# Revit family: AA-14FBS
name_source: partatom
category: Устройства связи
units: mm (PartAtom-declared; Revit-internal decimal feet)

## family parameters
Всегда вертикально = Нет
На основе рабочей плоскости = Да
Общий = Да
При загрузке вырезать с полостями = Нет
Размер круглого соединителя = Использовать диаметр
Сохранять ориентацию аннотаций = Нет
Тип детали = Нормальный
Точка расчета площади = Нет

## types (1)
- AA-14FBS
    ADSK_URL документации изделия = https://cdn.bas-ip.com
    ADSK_URL страницы изделия = https://bas-ip.com
    ADSK_Версия Revit = Revit 2020
    ADSK_Единица измерения = шт.
    ADSK_Завод-изготовитель = BAS-IP
    ADSK_Классификация нагрузок = Вызывная панель
    ADSK_Количество фаз = 1
    ADSK_Марка = AA-14FBS
    ADSK_Наименование = ВЫЗЫВНАЯ ПАНЕЛЬ AA-14FBS
    ADSK_Напряжение = 12 В
    ADSK_Номинальная мощность = 7 Вт
    IK-код = IK06
    URL = https://www.bas-ip.ru
    Аутентификация = Отдельный пароль для настроек WEB-интерфейса
    Выходное видео = Full HD (1920х1080), H.264 Main Profile
    Дисплей = 10, IPS, цветная с подсветкой и подогревом
    Дополнительно = Поддержка ПО Link, SIP P2P, Встроенное реле, Датчик приближения, API
    Изготовитель = BAS-IP
    Изображение типоразмера = <Нет>
    Интеграция со СКУД = Выход WIEGAND-26+
    Интерфейс = Многоязычный графическийи WEB-интерфейс
    Камера = 1/4”
    Класс степени защиты = IP65
    Кнопки быстрого вызова = Кнопка вызова консьержа
    Количество мелодий вызова = 4 полифонические мелодии, возможность настройки
    Контроль доступа = Распознавание лиц, UKEY (EM-Marin / MIFARE® / NFC / Bluetooth), Многофакторная аутентификация
    Корпус = Алюминий
    Минимальная освещенность = 0,01 LuX
    Ночная подсветка = 6 светодиодов
    Открытие замка = С помощью монитора, Идентификация с распознаванием лиц, По QR-коду, По гостевой ссылке, По PIN-коду, По карте доступа, По номерным знакам, Приложение BAS-IP Link, Приложение BAS-IP Intercom, Приложение BAS-IP UKEY, Из API
    Отметка по умолчанию = 0 мм
    Питание = +12 В DC
    Потребление питания = 6,5 Вт, в режиме ожидания – 3,6 Вт
    Размер под установку (кронштейна) = 172×373×58 мм
    Размер самой панели = 185×400×45 мм
    Разрешение камеры = 2 Мп
    Режим разговора = Двухсторонний
    Температурный режим = -40 ... +65 °С
    Тип клавиатуры = Сенсорная
    Тип панели = Многоквартирная
    Тип установки = Врезная, накладная с BR-AA
    Угол обзора = По горизонтали 110°
    Цветовое решение = Золото, серебро, черный
